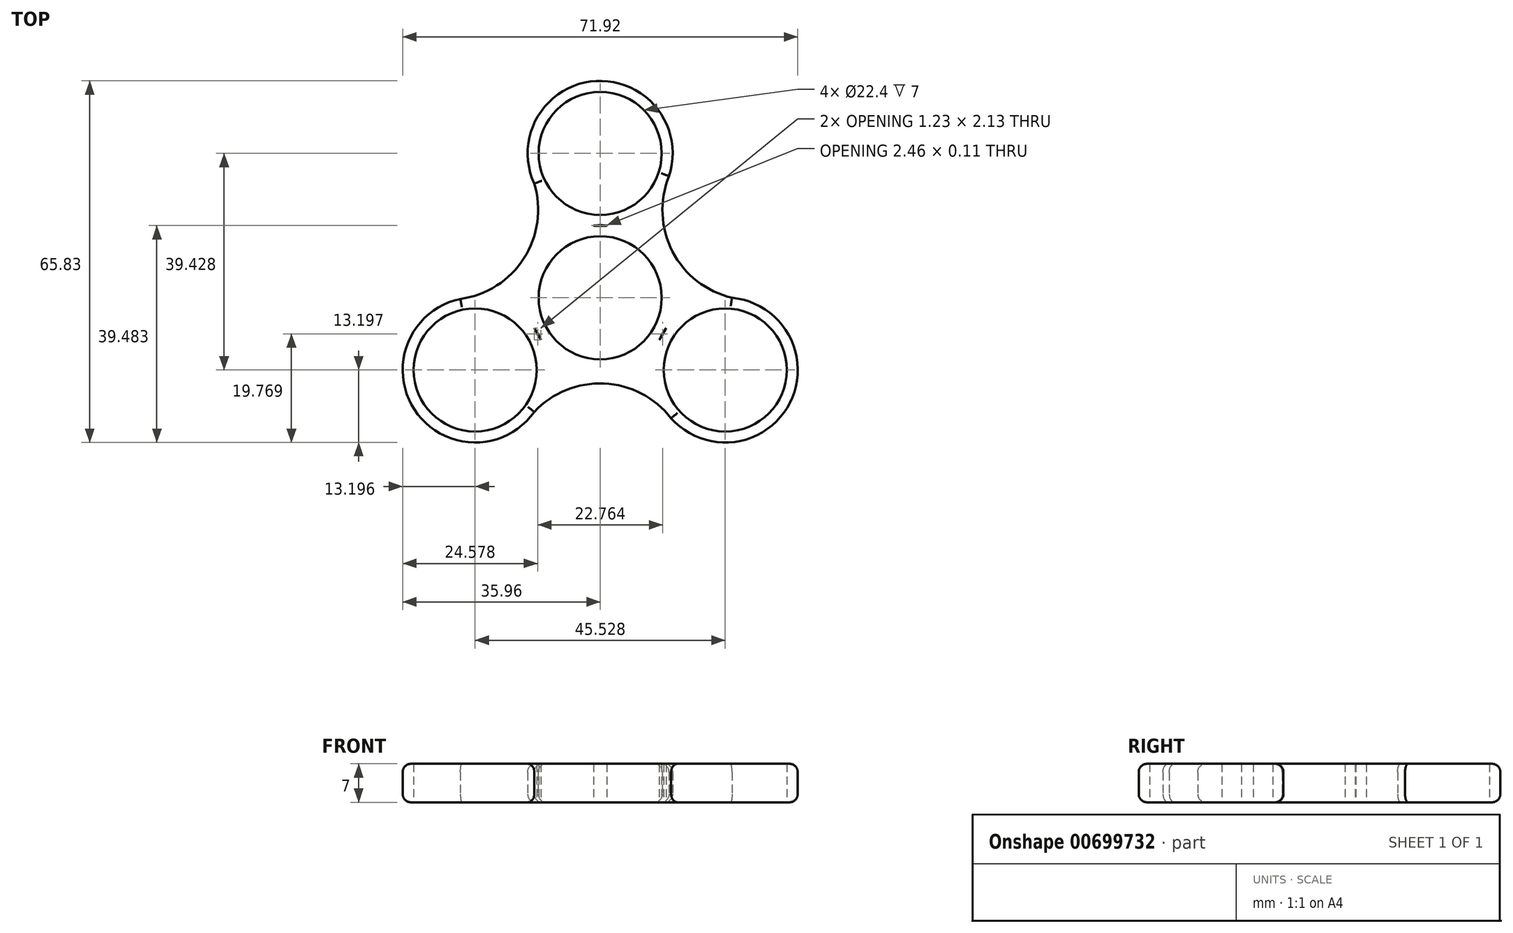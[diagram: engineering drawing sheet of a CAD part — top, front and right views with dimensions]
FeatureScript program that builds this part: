
annotation { "Feature Type Name" : "Feature", "Feature Type Description" : "" }
export const myFeature = defineFeature(function(context is Context, id is Id, definition is map)
    precondition{}
    {
        {
            var Q0;
            Q0=qCreatedBy(makeId("Top.planeOp"),FACE);
            var sketch = newSketch(context, id + "F0", { "sketchPlane" : qUnion([Q0])});
            skCircle(sketch, "E0", {"center": v(0, 0) * mm, "radius": 11.2 * mm});
            skArc(sketch, "E1", {"start": v(-12, -5.5) * mm, "mid": v(-11.43, -6.6) * mm, "end": v(-10.77, -7.64) * mm});
            skCircle(sketch, "E2", {"center": v(0, 26.29) * mm, "radius": 11.2 * mm});
            skArc(sketch, "E3", {"start": v(-1.23, 13.14) * mm, "mid": v(0, 13.09) * mm, "end": v(1.23, 13.14) * mm});
            skCircle(sketch, "E4.1.0", {"center": v(-22.76, -13.14) * mm, "radius": 11.2 * mm});
            skArc(sketch, "E4.1.1", {"start": v(-10.77, -7.64) * mm, "mid": v(-11.33, -6.54) * mm, "end": v(-12, -5.5) * mm});
            skCircle(sketch, "E4.2.0", {"center": v(22.76, -13.14) * mm, "radius": 11.2 * mm});
            skArc(sketch, "E4.2.1", {"start": v(12, -5.5) * mm, "mid": v(11.33, -6.54) * mm, "end": v(10.77, -7.64) * mm});
            skArc(sketch, "E5", {"start": v(12.53, 22.14) * mm, "mid": v(13.16, 8.43) * mm, "end": v(24, 0) * mm});
            skArc(sketch, "E6.1.0", {"start": v(-25.44, -0.22) * mm, "mid": v(-13.88, 7.18) * mm, "end": v(-12, 20.78) * mm});
            skArc(sketch, "E6.2.0", {"start": v(12.91, -21.93) * mm, "mid": v(0.72, -15.6) * mm, "end": v(-12, -20.78) * mm});
            skArc(sketch, "E7.trimOffspring", {"start": v(12.19, 21.22) * mm, "mid": v(-0.24, 39.48) * mm, "end": v(-12, 20.78) * mm});
            skArc(sketch, "E8.trimOffspring", {"start": v(12.28, -21.17) * mm, "mid": v(34.31, -19.53) * mm, "end": v(24, 0) * mm});
            skArc(sketch, "E9.trimOffspring", {"start": v(-24.47, -0.05) * mm, "mid": v(-34.07, -19.95) * mm, "end": v(-12, -20.78) * mm});
            skArc(sketch, "E10.trimOffspring", {"start": v(1.23, 13.14) * mm, "mid": v(0, 13.2) * mm, "end": v(-1.23, 13.14) * mm});
            skArc(sketch, "E11.trimOffspring", {"start": v(10.77, -7.64) * mm, "mid": v(11.43, -6.6) * mm, "end": v(12, -5.5) * mm});
            skSolve(sketch);
        }
        {
            var Q0;
            Q0=makeQuery(id+"F0.imprint","IMPRINT",FACE,{"disambiguationData":[TD([[makeQuery(id+"F0.imprint","IMPRINT",EDGE,{"derivedFrom":sQuery(id+"F0.wireOp",EDGE,"E0")}),-1.0]])]});
            extrude(context, id + "F1", {"entities" : qUnion([Q0]), "depth" : 7 * mm, "offsetDistance" : 25 * mm});
        }
        {
            var Q0;
            Q0=makeQuery(id+"F1.opExtrude","CAP_EDGE",EDGE,{"disambiguationData":[OSD([sQuery(id+"F0.wireOp",EDGE,"E6.2.0")])],"isStart":false});
            var Q1;
            Q1=makeQuery(id+"F1.opExtrude","CAP_EDGE",EDGE,{"disambiguationData":[OSD([sQuery(id+"F0.wireOp",EDGE,"E9.trimOffspring")])],"isStart":false});
            var Q2;
            Q2=makeQuery(id+"F1.opExtrude","CAP_EDGE",EDGE,{"disambiguationData":[OSD([sQuery(id+"F0.wireOp",EDGE,"E6.1.0")])],"isStart":false});
            var Q3;
            Q3=makeQuery(id+"F1.opExtrude","CAP_EDGE",EDGE,{"disambiguationData":[OSD([sQuery(id+"F0.wireOp",EDGE,"E7.trimOffspring")])],"isStart":false});
            var Q4;
            Q4=makeQuery(id+"F1.opExtrude","CAP_EDGE",EDGE,{"disambiguationData":[OSD([sQuery(id+"F0.wireOp",EDGE,"E5")])],"isStart":false});
            var Q5;
            Q5=makeQuery(id+"F1.opExtrude","CAP_EDGE",EDGE,{"disambiguationData":[OSD([sQuery(id+"F0.wireOp",EDGE,"E8.trimOffspring")])],"isStart":false});
            var Q6;
            Q6=makeQuery(id+"F1.opExtrude","CAP_EDGE",EDGE,{"disambiguationData":[OSD([sQuery(id+"F0.wireOp",EDGE,"E8.trimOffspring")])],"isStart":true});
            var Q7;
            Q7=makeQuery(id+"F1.opExtrude","CAP_EDGE",EDGE,{"disambiguationData":[OSD([sQuery(id+"F0.wireOp",EDGE,"E6.2.0")])],"isStart":true});
            var Q8;
            Q8=makeQuery(id+"F1.opExtrude","CAP_EDGE",EDGE,{"disambiguationData":[OSD([sQuery(id+"F0.wireOp",EDGE,"E9.trimOffspring")])],"isStart":true});
            var Q9;
            Q9=makeQuery(id+"F1.opExtrude","CAP_EDGE",EDGE,{"disambiguationData":[OSD([sQuery(id+"F0.wireOp",EDGE,"E5")])],"isStart":true});
            var Q10;
            Q10=makeQuery(id+"F1.opExtrude","CAP_EDGE",EDGE,{"disambiguationData":[OSD([sQuery(id+"F0.wireOp",EDGE,"E7.trimOffspring")])],"isStart":true});
            var Q11;
            Q11=makeQuery(id+"F1.opExtrude","CAP_EDGE",EDGE,{"disambiguationData":[OSD([sQuery(id+"F0.wireOp",EDGE,"E6.1.0")])],"isStart":true});
            fillet(context, id + "F2", {"entities" : qUnion([Q0, Q1, Q2, Q3, Q4, Q5, Q6, Q7, Q8, Q9, Q10, Q11]), "radius" : 1.5 * mm, "tangentPropagation" : true, "allowEdgeOverflow" : false});
        }
    });
